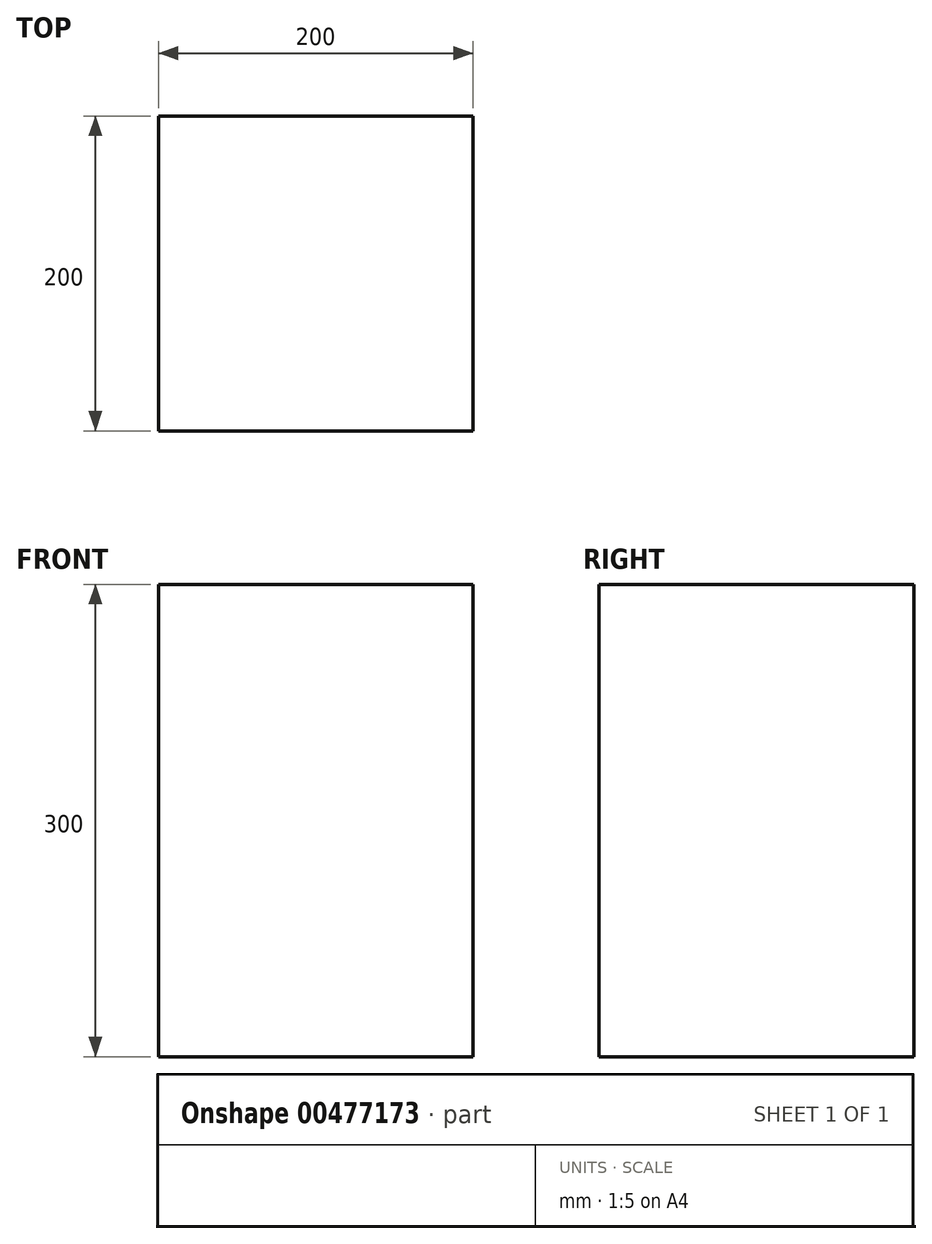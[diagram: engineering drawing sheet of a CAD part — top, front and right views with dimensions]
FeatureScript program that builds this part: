
annotation { "Feature Type Name" : "Feature", "Feature Type Description" : "" }
export const myFeature = defineFeature(function(context is Context, id is Id, definition is map)
    precondition{}
    {
        {
            var Q0;
            Q0=qCreatedBy(makeId("Top.planeOp"),FACE);
            var sketch = newSketch(context, id + "F0", { "sketchPlane" : qUnion([Q0])});
            skLineSegment(sketch, "E0.bottom", {"start": v(100, -100) * mm, "end": v(-100, -100) * mm});
            skLineSegment(sketch, "E0.top", {"start": v(100, 100) * mm, "end": v(-100, 100) * mm});
            skLineSegment(sketch, "E0.left", {"start": v(100, -100) * mm, "end": v(100, 100) * mm});
            skLineSegment(sketch, "E0.right", {"start": v(-100, -100) * mm, "end": v(-100, 100) * mm});
            skPoint(sketch, "E0.middle", {"position": v(0, 0) * mm});
            skSolve(sketch);
        }
        {
            var Q0;
            Q0=makeQuery(id+"F0.imprint","IMPRINT",FACE,{"disambiguationData":[TD([[makeQuery(id+"F0.imprint","IMPRINT",EDGE,{"derivedFrom":sQuery(id+"F0.wireOp",EDGE,"E0.bottom")}),-1.0]])]});
            extrude(context, id + "F1", {"entities" : qUnion([Q0]), "depth" : 300 * mm});
        }
    });
